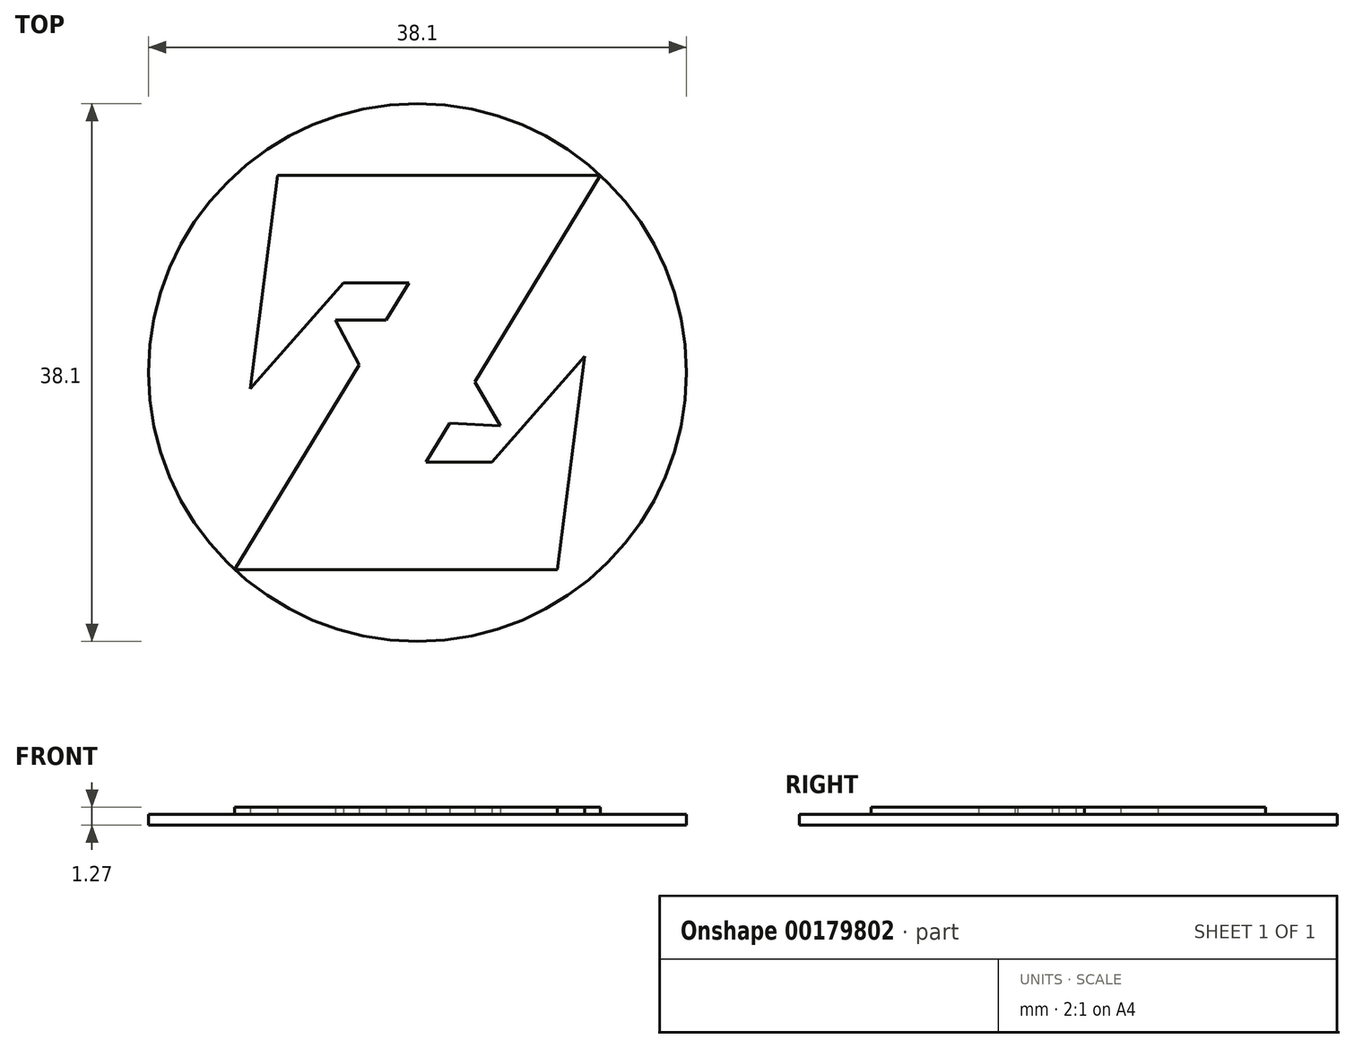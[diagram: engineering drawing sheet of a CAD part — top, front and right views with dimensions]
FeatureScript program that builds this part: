
annotation { "Feature Type Name" : "Feature", "Feature Type Description" : "" }
export const myFeature = defineFeature(function(context is Context, id is Id, definition is map)
    precondition{}
    {
        {
            var Q0;
            Q0=qCreatedBy(makeId("Top.planeOp"),FACE);
            var sketch = newSketch(context, id + "F0", { "sketchPlane" : qUnion([Q0])});
            skCircle(sketch, "E0", {"center": v(0, 0) * mm, "radius": 19.05 * mm});
            skSolve(sketch);
        }
        {
            var Q0;
            Q0 = qSketchRegion(id + "F0", true);
            extrude(context, id + "F1", {"entities" : qUnion([Q0]), "depth" : 0.76 * mm});
        }
        {
            var Q0;
            Q0=makeQuery(id+"F1.opExtrude","CAP_FACE",FACE,{"disambiguationData":[OSD([sQuery(id+"F0.wireOp",EDGE,"E0")])],"isStart":false});
            var sketch = newSketch(context, id + "F2", { "sketchPlane" : qUnion([Q0])});
            skLineSegment(sketch, "E1", {"start": v(-9.9, 13.97) * mm, "end": v(12.95, 13.97) * mm});
            skLineSegment(sketch, "E2", {"start": v(12.95, 13.97) * mm, "end": v(4.05, -0.67) * mm});
            skLineSegment(sketch, "E3", {"start": v(0.6, -6.35) * mm, "end": v(5.25, -6.35) * mm});
            skLineSegment(sketch, "E4", {"start": v(9.9, -6.35) * mm, "end": v(9.9, -13.97) * mm, "construction": true});
            skLineSegment(sketch, "E5", {"start": v(9.9, -13.97) * mm, "end": v(-12.95, -13.97) * mm});
            skLineSegment(sketch, "E6", {"start": v(-12.95, -13.97) * mm, "end": v(-4.13, 0.54) * mm});
            skLineSegment(sketch, "E7", {"start": v(-0.6, 6.35) * mm, "end": v(-5.25, 6.35) * mm});
            skLineSegment(sketch, "E8", {"start": v(-9.9, 6.35) * mm, "end": v(-9.9, 13.97) * mm, "construction": true});
            skLineSegment(sketch, "E9", {"start": v(-5.25, 6.35) * mm, "end": v(-11.84, -1.15) * mm});
            skLineSegment(sketch, "E10", {"start": v(-11.84, -1.15) * mm, "end": v(-9.9, 13.97) * mm});
            skLineSegment(sketch, "E11", {"start": v(5.25, -6.35) * mm, "end": v(11.84, 1.15) * mm});
            skLineSegment(sketch, "E12", {"start": v(11.84, 1.15) * mm, "end": v(9.9, -13.97) * mm});
            skLineSegment(sketch, "E13", {"start": v(0, 0) * mm, "end": v(9.9, -6.35) * mm, "construction": true});
            skLineSegment(sketch, "E14", {"start": v(0, 0) * mm, "end": v(-9.9, 6.35) * mm, "construction": true});
            skLineSegment(sketch, "E15", {"start": v(-4.13, 0.54) * mm, "end": v(-5.81, 3.72) * mm});
            skLineSegment(sketch, "E16", {"start": v(-5.81, 3.72) * mm, "end": v(-2.2, 3.7) * mm});
            skLineSegment(sketch, "E17", {"start": v(4.05, -0.67) * mm, "end": v(5.88, -3.77) * mm});
            skLineSegment(sketch, "E18", {"start": v(5.88, -3.77) * mm, "end": v(2.28, -3.58) * mm});
            skLineSegment(sketch, "E19", {"start": v(2.28, -3.58) * mm, "end": v(-4.13, 0.54) * mm, "construction": true});
            skLineSegment(sketch, "E20.trimOffspring", {"start": v(2.28, -3.58) * mm, "end": v(0.6, -6.35) * mm});
            skLineSegment(sketch, "E21.trimOffspring", {"start": v(-2.2, 3.7) * mm, "end": v(-0.6, 6.35) * mm});
            skSolve(sketch);
        }
        {
            var Q0;
            Q0 = qSketchRegion(id + "F2", true);
            extrude(context, id + "F3", {"entities" : qUnion([Q0]), "depth" : 0.5 * mm});
        }
    });
